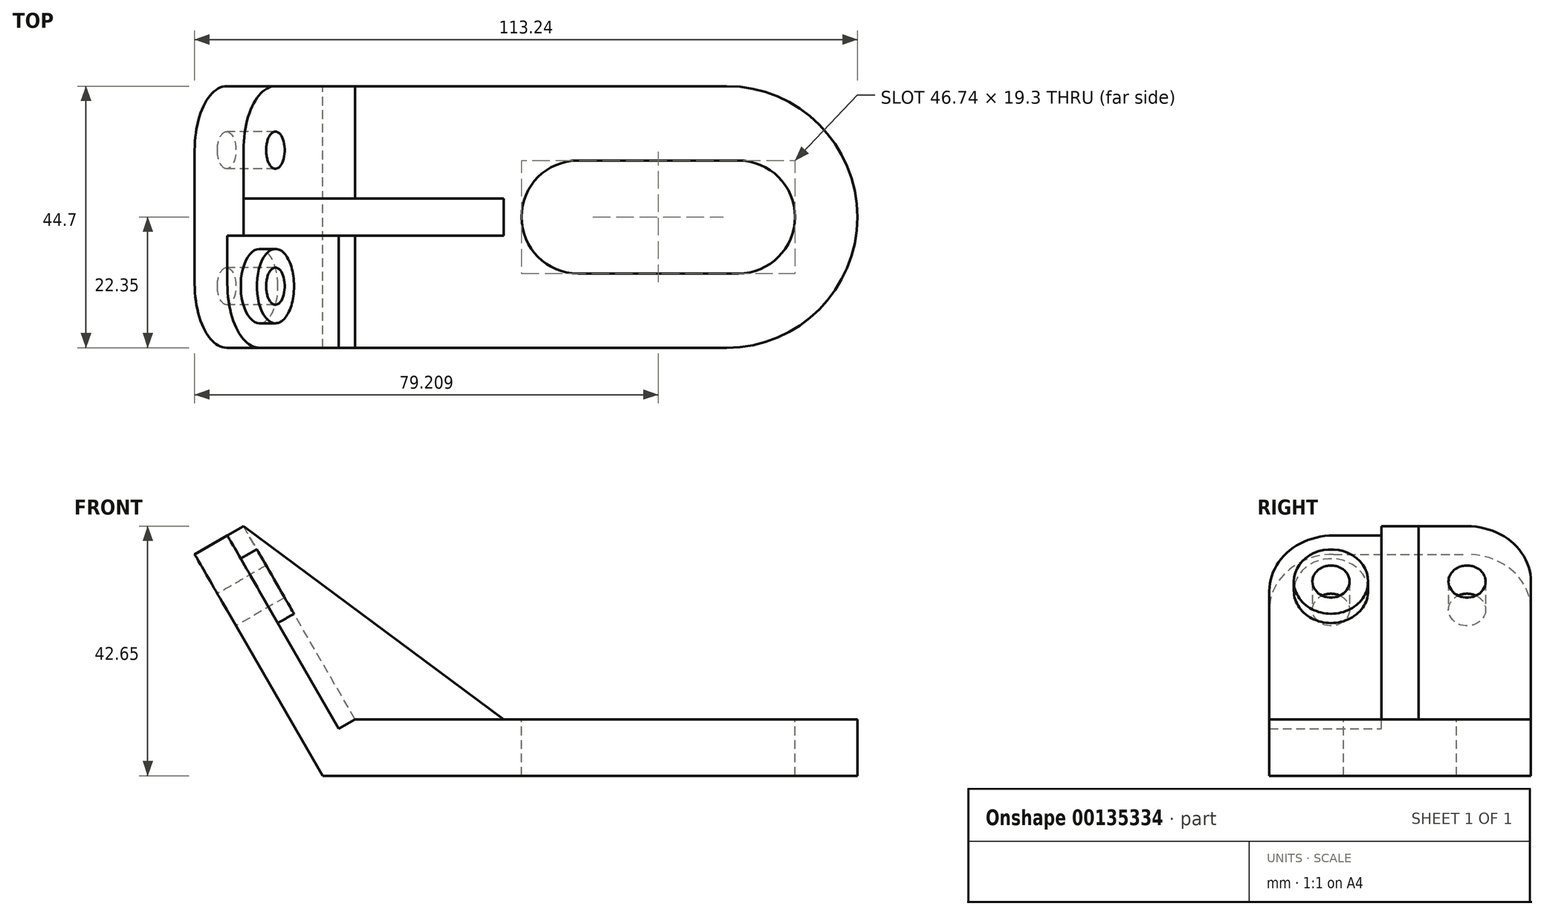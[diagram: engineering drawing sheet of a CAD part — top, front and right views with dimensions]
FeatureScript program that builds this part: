
annotation { "Feature Type Name" : "Feature", "Feature Type Description" : "" }
export const myFeature = defineFeature(function(context is Context, id is Id, definition is map)
    precondition{}
    {
        {
            var Q0;
            Q0=qCreatedBy(makeId("Front.planeOp"),FACE);
            var sketch = newSketch(context, id + "F0", { "sketchPlane" : qUnion([Q0])});
            skLineSegment(sketch, "E0", {"start": v(-25.4, 0) * mm, "end": v(-44.45, 33) * mm});
            skLineSegment(sketch, "E1", {"start": v(-44.45, 33) * mm, "end": v(-52.79, 28.18) * mm});
            skLineSegment(sketch, "E2", {"start": v(-52.79, 28.18) * mm, "end": v(-30.94, -9.65) * mm});
            skLineSegment(sketch, "E3", {"start": v(-44.45, 33) * mm, "end": v(0, 0) * mm});
            skLineSegment(sketch, "E4", {"start": v(-25.4, 0) * mm, "end": v(60.45, 0) * mm});
            skLineSegment(sketch, "E5", {"start": v(-30.94, -9.65) * mm, "end": v(60.45, -9.65) * mm});
            skLineSegment(sketch, "E6", {"start": v(60.45, 0) * mm, "end": v(60.45, -9.65) * mm});
            skSolve(sketch);
        }
        {
            var Q0;
            {var subQ0=sQuery(id+"F0.wireOp",EDGE,"E0");Q0=makeQuery(id+"F0.imprint","IMPRINT",FACE,{"disambiguationData":[TD([[makeQuery(id+"F0.imprint","IMPRINT",EDGE,{"derivedFrom":subQ0}),1.0]])]});}
            extrude(context, id + "F1", {"entities" : qUnion([Q0]), "endBound" : BoundingType.SYMMETRIC, "depth" : 44.7 * mm});
        }
        {
            var Q0;
            {var subQ0=sQuery(id+"F0.wireOp",EDGE,"E0");Q0=makeQuery(id+"F0.imprint","IMPRINT",FACE,{"disambiguationData":[TD([[makeQuery(id+"F0.imprint","IMPRINT",EDGE,{"derivedFrom":subQ0}),-1.0]])]});}
            extrude(context, id + "F2", {"entities" : qUnion([Q0]), "operationType" : NewBodyOperationType.ADD, "endBound" : BoundingType.SYMMETRIC, "depth" : 6.35 * mm});
        }
        {
            var Q0;
            Q0=makeQuery(id+"F1.opExtrude","SWEPT_FACE",FACE,{"disambiguationData":[OSD([sQuery(id+"F0.wireOp",EDGE,"E4")])]});
            var sketch = newSketch(context, id + "F3", { "sketchPlane" : qUnion([Q0])});
            skLineSegment(sketch, "E7", {"start": v(12.7, -9.65) * mm, "end": v(40.14, -9.65) * mm});
            skLineSegment(sketch, "E8", {"start": v(12.7, 9.65) * mm, "end": v(40.14, 9.65) * mm});
            skArc(sketch, "E9", {"start": v(12.7, 9.65) * mm, "mid": v(3.05, 0) * mm, "end": v(12.7, -9.65) * mm});
            skArc(sketch, "E10", {"start": v(40.14, -9.65) * mm, "mid": v(49.8, 0) * mm, "end": v(40.14, 9.65) * mm});
            skSolve(sketch);
        }
        {
            var Q0;
            Q0=makeQuery(id+"F1.opExtrude","CAP_EDGE",EDGE,{"disambiguationData":[OSD([sQuery(id+"F0.wireOp",EDGE,"E6")])],"isStart":false});
            var Q1;
            Q1=makeQuery(id+"F1.opExtrude","CAP_EDGE",EDGE,{"disambiguationData":[OSD([sQuery(id+"F0.wireOp",EDGE,"E6")])],"isStart":true});
            fillet(context, id + "F4", {"entities" : qUnion([Q0, Q1]), "radius" : 22.35 * mm, "tangentPropagation" : true, "allowEdgeOverflow" : false});
        }
        {
            var Q0;
            Q0=makeQuery(id+"F3.imprint","IMPRINT",FACE,{"disambiguationData":[TD([[makeQuery(id+"F3.imprint","IMPRINT",EDGE,{"derivedFrom":sQuery(id+"F3.wireOp",EDGE,"E7")}),1.0]])]});
            extrude(context, id + "F5", {"entities" : qUnion([Q0]), "operationType" : NewBodyOperationType.REMOVE, "oppositeDirection" : true, "depth" : 25.4 * mm});
        }
        {
            var Q0;
            Q0=makeQuery(id+"F1.opExtrude","SWEPT_FACE",FACE,{"disambiguationData":[OSD([sQuery(id+"F0.wireOp",EDGE,"E2")])]});
            var sketch = newSketch(context, id + "F6", { "sketchPlane" : qUnion([Q0])});
            skCircle(sketch, "E11", {"center": v(-11.43, 39.88) * mm, "radius": 3.18 * mm});
            skCircle(sketch, "E12", {"center": v(-11.43, 39.88) * mm, "radius": 6.35 * mm});
            skCircle(sketch, "E13", {"center": v(11.81, 39.88) * mm, "radius": 3.18 * mm});
            skCircle(sketch, "E14", {"center": v(11.81, 39.88) * mm, "radius": 6.35 * mm});
            skSolve(sketch);
        }
        {
            var Q0;
            Q0=makeQuery(id+"F6.imprint","IMPRINT",FACE,{"disambiguationData":[TD([[makeQuery(id+"F6.imprint","IMPRINT",EDGE,{"derivedFrom":sQuery(id+"F6.wireOp",EDGE,"E13")}),1.0]])]});
            var Q1;
            Q1=makeQuery(id+"F6.imprint","IMPRINT",FACE,{"disambiguationData":[TD([[makeQuery(id+"F6.imprint","IMPRINT",EDGE,{"derivedFrom":sQuery(id+"F6.wireOp",EDGE,"E11")}),1.0]])]});
            extrude(context, id + "F7", {"entities" : qUnion([Q0, Q1]), "operationType" : NewBodyOperationType.REMOVE, "oppositeDirection" : true, "depth" : 25.4 * mm});
        }
        {
            var Q0;
            {var subQ0=sQuery(id+"F0.wireOp",EDGE,"E4");var subQ1=sQuery(id+"F0.wireOp",EDGE,"E3");var subQ2=sQuery(id+"F0.wireOp",EDGE,"E0");Q0=makeQuery(id+"F2.boolean.opBoolean","SPLIT",FACE,{"disambiguationData":[TD([makeQuery(id+"F2.opExtrude","CAP_FACE",FACE,{"disambiguationData":[OSD([subQ2,subQ1,subQ0])],"isStart":false})])],"derivedFrom":makeQuery(id+"F1.opExtrude","SWEPT_FACE",FACE,{"disambiguationData":[OSD([subQ2])]})});}
            var sketch = newSketch(context, id + "F8", { "sketchPlane" : qUnion([Q0])});
            skCircle(sketch, "E15.0", {"center": v(-11.81, 39.88) * mm, "radius": 6.35 * mm});
            skCircle(sketch, "E16.0", {"center": v(11.43, 39.88) * mm, "radius": 6.35 * mm});
            skSolve(sketch);
        }
        {
            var Q0;
            Q0=makeQuery(id+"F8.imprint","IMPRINT",FACE,{"disambiguationData":[TD([[makeQuery(id+"F8.imprint","IMPRINT",EDGE,{"derivedFrom":sQuery(id+"F8.wireOp",EDGE,"E15.0")}),-1.0]])]});
            var Q1;
            Q1=makeQuery(id+"F8.imprint","IMPRINT",FACE,{"disambiguationData":[TD([[makeQuery(id+"F8.imprint","IMPRINT",EDGE,{"derivedFrom":sQuery(id+"F8.wireOp",EDGE,"E16.0")}),-1.0]])]});
            extrude(context, id + "F9", {"entities" : qUnion([Q0, Q1]), "operationType" : NewBodyOperationType.REMOVE, "oppositeDirection" : true, "depth" : 3.17 * mm});
        }
        {
            var Q0;
            Q0=makeQuery(id+"F1.opExtrude","CAP_EDGE",EDGE,{"disambiguationData":[OSD([sQuery(id+"F0.wireOp",EDGE,"E1")])],"isStart":false});
            var Q1;
            Q1=makeQuery(id+"F1.opExtrude","CAP_EDGE",EDGE,{"disambiguationData":[OSD([sQuery(id+"F0.wireOp",EDGE,"E1")])],"isStart":true});
            fillet(context, id + "F10", {"entities" : qUnion([Q0, Q1]), "radius" : 10.92 * mm, "tangentPropagation" : true, "allowEdgeOverflow" : false});
        }
    });
